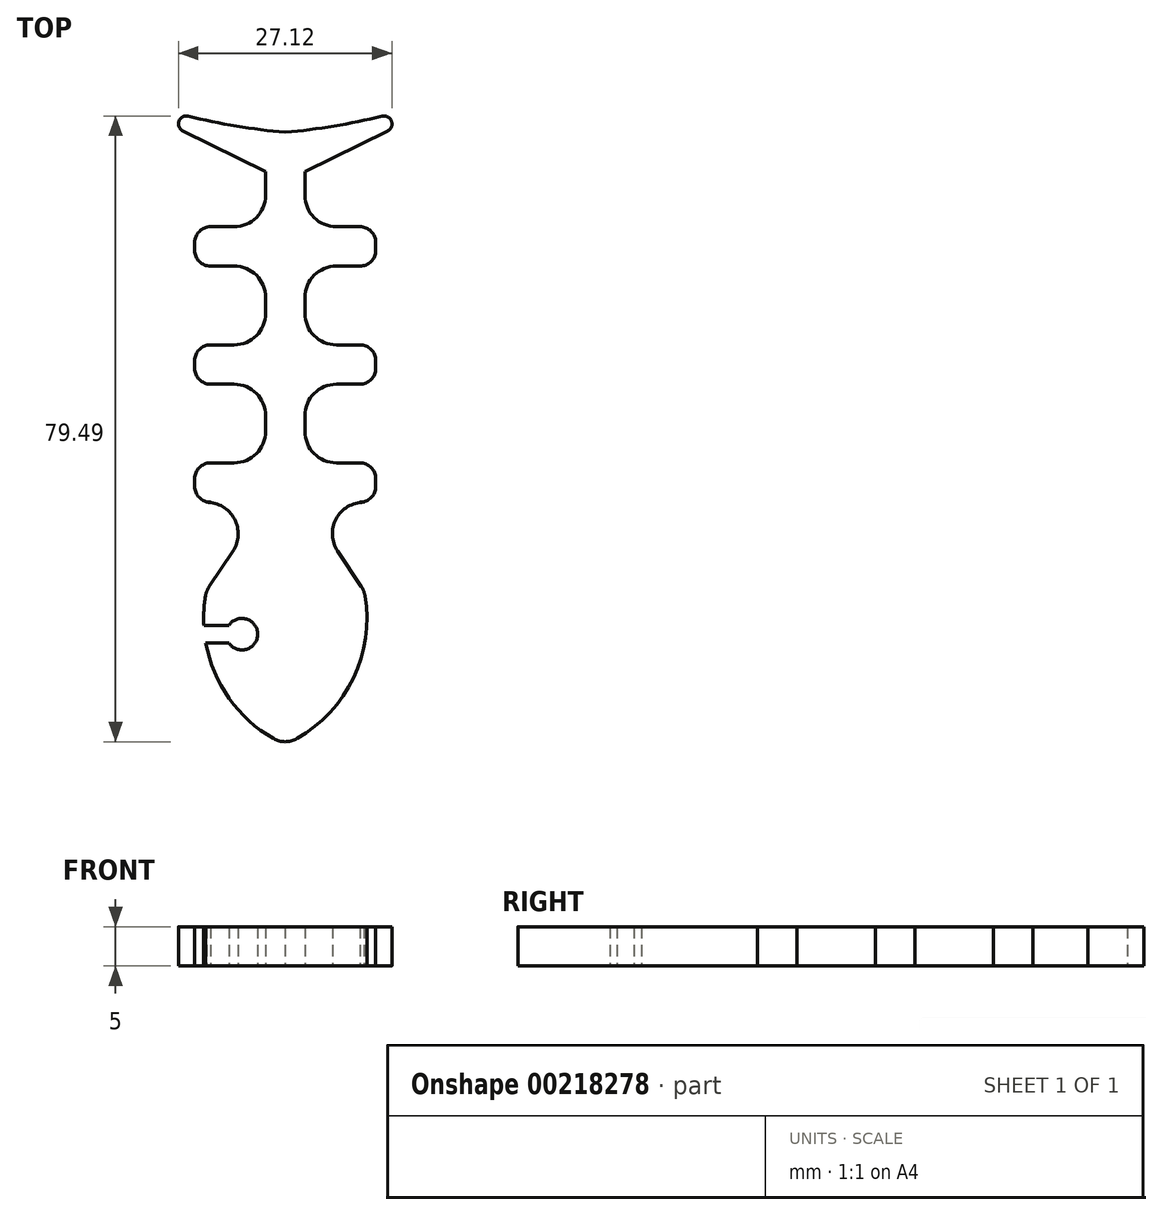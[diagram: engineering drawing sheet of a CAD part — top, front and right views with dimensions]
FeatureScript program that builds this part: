
annotation { "Feature Type Name" : "Feature", "Feature Type Description" : "" }
export const myFeature = defineFeature(function(context is Context, id is Id, definition is map)
    precondition{}
    {
        {
            var Q0;
            Q0=qCreatedBy(makeId("Top.planeOp"),FACE);
            var sketch = newSketch(context, id + "F0", { "sketchPlane" : qUnion([Q0])});
            skLineSegment(sketch, "E0", {"start": v(0, -19.65) * mm, "end": v(0, 37) * mm});
            skLineSegment(sketch, "E1", {"start": v(-9.66, -15.71) * mm, "end": v(-6.66, -11.22) * mm});
            skLineSegment(sketch, "E2", {"start": v(-9.5, -5) * mm, "end": v(-9.98, -5) * mm});
            skLineSegment(sketch, "E3", {"start": v(-11.5, -3) * mm, "end": v(-11.5, -2) * mm});
            skLineSegment(sketch, "E4", {"start": v(-9.5, 0) * mm, "end": v(-6.5, 0) * mm});
            skLineSegment(sketch, "E5", {"start": v(-2.5, 4) * mm, "end": v(-2.5, 6) * mm});
            skLineSegment(sketch, "E6", {"start": v(-6.5, 10) * mm, "end": v(-9.5, 10) * mm});
            skLineSegment(sketch, "E7", {"start": v(-11.5, 12) * mm, "end": v(-11.5, 13) * mm});
            skLineSegment(sketch, "E8", {"start": v(-9.5, 15) * mm, "end": v(-6.5, 15) * mm});
            skLineSegment(sketch, "E9", {"start": v(-2.5, 19) * mm, "end": v(-2.5, 21) * mm});
            skLineSegment(sketch, "E10", {"start": v(-6.5, 25) * mm, "end": v(-9.5, 25) * mm});
            skLineSegment(sketch, "E11", {"start": v(-11.5, 27) * mm, "end": v(-11.5, 28) * mm});
            skLineSegment(sketch, "E12", {"start": v(-9.5, 30) * mm, "end": v(-6.5, 30) * mm});
            skLineSegment(sketch, "E13", {"start": v(-2.5, 34) * mm, "end": v(-2.5, 37) * mm});
            skLineSegment(sketch, "E14", {"start": v(-2.5, 37) * mm, "end": v(-13, 42.17) * mm});
            skLineSegment(sketch, "E15", {"start": v(0, 37) * mm, "end": v(0, 42) * mm});
            skArc(sketch, "E16", {"start": v(-12.32, 44.04) * mm, "mid": v(-6.2, 42.79) * mm, "end": v(0, 42) * mm});
            skLineSegment(sketch, "E17", {"start": v(0, -19.65) * mm, "end": v(0, -23.17) * mm});
            skPoint(sketch, "E18.visualSharp", {"position": v(-2.5, 30) * mm});
            skArc(sketch, "E18.filletArc", {"start": v(-6.5, 30) * mm, "mid": v(-3.67, 31.17) * mm, "end": v(-2.5, 34) * mm});
            skPoint(sketch, "E19.visualSharp", {"position": v(-2.5, 25) * mm});
            skArc(sketch, "E19.filletArc", {"start": v(-2.5, 21) * mm, "mid": v(-3.67, 23.83) * mm, "end": v(-6.5, 25) * mm});
            skPoint(sketch, "E20.visualSharp", {"position": v(-2.5, 15) * mm});
            skArc(sketch, "E20.filletArc", {"start": v(-6.5, 15) * mm, "mid": v(-3.67, 16.17) * mm, "end": v(-2.5, 19) * mm});
            skPoint(sketch, "E21.visualSharp", {"position": v(-2.5, 10) * mm});
            skArc(sketch, "E21.filletArc", {"start": v(-2.5, 6) * mm, "mid": v(-3.67, 8.83) * mm, "end": v(-6.5, 10) * mm});
            skPoint(sketch, "E22.visualSharp", {"position": v(-2.5, 0) * mm});
            skArc(sketch, "E22.filletArc", {"start": v(-6.5, 0) * mm, "mid": v(-3.67, 1.17) * mm, "end": v(-2.5, 4) * mm});
            skPoint(sketch, "E23.visualSharp", {"position": v(-2.5, -5) * mm});
            skArc(sketch, "E23.filletArc", {"start": v(-6.66, -11.22) * mm, "mid": v(-6.46, -7.11) * mm, "end": v(-9.98, -5) * mm});
            skPoint(sketch, "E24.visualSharp", {"position": v(-11.5, 30) * mm});
            skArc(sketch, "E24.filletArc", {"start": v(-9.5, 30) * mm, "mid": v(-10.91, 29.41) * mm, "end": v(-11.5, 28) * mm});
            skPoint(sketch, "E25.visualSharp", {"position": v(-11.5, 15) * mm});
            skArc(sketch, "E25.filletArc", {"start": v(-9.5, 15) * mm, "mid": v(-10.91, 14.41) * mm, "end": v(-11.5, 13) * mm});
            skPoint(sketch, "E26.visualSharp", {"position": v(-11.5, 0) * mm});
            skArc(sketch, "E26.filletArc", {"start": v(-9.5, 0) * mm, "mid": v(-10.91, -0.59) * mm, "end": v(-11.5, -2) * mm});
            skPoint(sketch, "E27.visualSharp", {"position": v(-11.5, 25) * mm});
            skArc(sketch, "E27.filletArc", {"start": v(-11.5, 27) * mm, "mid": v(-10.91, 25.59) * mm, "end": v(-9.5, 25) * mm});
            skPoint(sketch, "E28.visualSharp", {"position": v(-11.5, 10) * mm});
            skArc(sketch, "E28.filletArc", {"start": v(-11.5, 12) * mm, "mid": v(-10.91, 10.59) * mm, "end": v(-9.5, 10) * mm});
            skPoint(sketch, "E29.visualSharp", {"position": v(-11.5, -5) * mm});
            skArc(sketch, "E29.filletArc", {"start": v(-11.5, -3) * mm, "mid": v(-10.91, -4.41) * mm, "end": v(-9.5, -5) * mm});
            skPoint(sketch, "E30.visualSharp", {"position": v(-28.2, 49.66) * mm});
            skArc(sketch, "E30.filletArc", {"start": v(-12.32, 44.04) * mm, "mid": v(-13.5, 43.41) * mm, "end": v(-13, 42.17) * mm});
            skArc(sketch, "E31.MirrorCS", {"start": v(9.5, 0) * mm, "mid": v(10.91, -0.59) * mm, "end": v(11.5, -2) * mm});
            skLineSegment(sketch, "E32.MirrorCS", {"start": v(11.5, 27) * mm, "end": v(11.5, 28) * mm});
            skLineSegment(sketch, "E33.MirrorCS", {"start": v(9.5, -5) * mm, "end": v(9.98, -5) * mm});
            skLineSegment(sketch, "E34.MirrorCS", {"start": v(11.5, 12) * mm, "end": v(11.5, 13) * mm});
            skLineSegment(sketch, "E35.MirrorCS", {"start": v(2.5, 4) * mm, "end": v(2.5, 6) * mm});
            skArc(sketch, "E36.MirrorCS", {"start": v(11.5, 12) * mm, "mid": v(10.91, 10.59) * mm, "end": v(9.5, 10) * mm});
            skArc(sketch, "E37.MirrorCS", {"start": v(11.5, -3) * mm, "mid": v(10.91, -4.41) * mm, "end": v(9.5, -5) * mm});
            skArc(sketch, "E38.MirrorCS", {"start": v(9.5, 30) * mm, "mid": v(10.91, 29.41) * mm, "end": v(11.5, 28) * mm});
            skLineSegment(sketch, "E39.MirrorCS", {"start": v(11.5, -3) * mm, "end": v(11.5, -2) * mm});
            skLineSegment(sketch, "E40.MirrorCS", {"start": v(2.5, 34) * mm, "end": v(2.5, 37) * mm});
            skArc(sketch, "E41.MirrorCS", {"start": v(12.32, 44.04) * mm, "mid": v(13.5, 43.41) * mm, "end": v(13, 42.17) * mm});
            skArc(sketch, "E42.MirrorCS", {"start": v(9.5, 15) * mm, "mid": v(10.91, 14.41) * mm, "end": v(11.5, 13) * mm});
            skLineSegment(sketch, "E43.MirrorCS", {"start": v(9.5, 15) * mm, "end": v(6.5, 15) * mm});
            skLineSegment(sketch, "E44.MirrorCS", {"start": v(6.5, 25) * mm, "end": v(9.5, 25) * mm});
            skLineSegment(sketch, "E45.MirrorCS", {"start": v(2.5, 19) * mm, "end": v(2.5, 21) * mm});
            skArc(sketch, "E46.MirrorCS", {"start": v(11.5, 27) * mm, "mid": v(10.91, 25.59) * mm, "end": v(9.5, 25) * mm});
            skLineSegment(sketch, "E47.MirrorCS", {"start": v(9.5, 30) * mm, "end": v(6.5, 30) * mm});
            skLineSegment(sketch, "E48.MirrorCS", {"start": v(6.5, 10) * mm, "end": v(9.5, 10) * mm});
            skLineSegment(sketch, "E49.MirrorCS", {"start": v(9.5, 0) * mm, "end": v(6.5, 0) * mm});
            skArc(sketch, "E50.MirrorCS", {"start": v(2.5, 21) * mm, "mid": v(3.67, 23.83) * mm, "end": v(6.5, 25) * mm});
            skArc(sketch, "E51.MirrorCS", {"start": v(6.5, 30) * mm, "mid": v(3.67, 31.17) * mm, "end": v(2.5, 34) * mm});
            skArc(sketch, "E52.MirrorCS", {"start": v(6.5, 0) * mm, "mid": v(3.67, 1.17) * mm, "end": v(2.5, 4) * mm});
            skArc(sketch, "E53.MirrorCS", {"start": v(6.66, -11.22) * mm, "mid": v(6.46, -7.11) * mm, "end": v(9.98, -5) * mm});
            skArc(sketch, "E54.MirrorCS", {"start": v(2.5, 6) * mm, "mid": v(3.67, 8.83) * mm, "end": v(6.5, 10) * mm});
            skArc(sketch, "E55.MirrorCS", {"start": v(6.5, 15) * mm, "mid": v(3.67, 16.17) * mm, "end": v(2.5, 19) * mm});
            skPoint(sketch, "E56.MirrorP", {"position": v(2.5, 25) * mm});
            skPoint(sketch, "E57.MirrorP", {"position": v(2.5, 0) * mm});
            skLineSegment(sketch, "E58.MirrorCS", {"start": v(2.5, 37) * mm, "end": v(13, 42.17) * mm});
            skPoint(sketch, "E59.MirrorP", {"position": v(11.5, 25) * mm});
            skPoint(sketch, "E60.MirrorP", {"position": v(11.5, 15) * mm});
            skLineSegment(sketch, "E61.MirrorCS", {"start": v(9.66, -15.71) * mm, "end": v(6.66, -11.22) * mm});
            skArc(sketch, "E62.MirrorCS", {"start": v(12.32, 44.04) * mm, "mid": v(6.2, 42.79) * mm, "end": v(0, 42) * mm});
            skPoint(sketch, "E63.MirrorP", {"position": v(11.5, -5) * mm});
            skPoint(sketch, "E64.MirrorP", {"position": v(2.5, 15) * mm});
            skPoint(sketch, "E65.MirrorP", {"position": v(2.5, 30) * mm});
            skPoint(sketch, "E66.MirrorP", {"position": v(11.5, 0) * mm});
            skPoint(sketch, "E67.MirrorP", {"position": v(11.5, 10) * mm});
            skPoint(sketch, "E68.MirrorP", {"position": v(2.5, 10) * mm});
            skPoint(sketch, "E69.MirrorP", {"position": v(2.5, -5) * mm});
            skPoint(sketch, "E70.MirrorP", {"position": v(11.5, 30) * mm});
            skArc(sketch, "E71", {"start": v(-10.12, -16.89) * mm, "mid": v(-10.33, -18.76) * mm, "end": v(-10.34, -20.65) * mm});
            skArc(sketch, "E72.MirrorCS", {"start": v(10.12, -16.89) * mm, "mid": v(8.66, -27.32) * mm, "end": v(1.48, -35.03) * mm});
            skPoint(sketch, "E73.visualSharp", {"position": v(0, -35.78) * mm});
            skArc(sketch, "E73.filletArc", {"start": v(-1.48, -35.03) * mm, "mid": v(0, -35.42) * mm, "end": v(1.48, -35.03) * mm});
            skPoint(sketch, "E74.visualSharp", {"position": v(10, -16.22) * mm});
            skArc(sketch, "E74.filletArc", {"start": v(10.12, -16.89) * mm, "mid": v(9.95, -16.27) * mm, "end": v(9.66, -15.71) * mm});
            skPoint(sketch, "E75.visualSharp", {"position": v(-10, -16.22) * mm});
            skArc(sketch, "E75.filletArc", {"start": v(-9.66, -15.71) * mm, "mid": v(-9.95, -16.27) * mm, "end": v(-10.12, -16.89) * mm});
            skArc(sketch, "E76", {"start": v(-7.16, -22.87) * mm, "mid": v(-3.5, -21.76) * mm, "end": v(-7.16, -20.65) * mm});
            skLineSegment(sketch, "E77", {"start": v(-7.16, -20.65) * mm, "end": v(-10.34, -20.65) * mm});
            skLineSegment(sketch, "E78", {"start": v(-7.16, -22.87) * mm, "end": v(-10.09, -22.87) * mm});
            skArc(sketch, "E79.trimOffspring", {"start": v(-10.09, -22.87) * mm, "mid": v(-7.14, -29.9) * mm, "end": v(-1.48, -35.03) * mm});
            skSolve(sketch);
        }
        {
            var Q0;
            Q0=makeQuery(id+"F0.imprint","IMPRINT",FACE,{"disambiguationData":[TD([[makeQuery(id+"F0.imprint","IMPRINT",EDGE,{"derivedFrom":sQuery(id+"F0.wireOp",EDGE,"E1")}),-1.0]])]});
            extrude(context, id + "F1", {"entities" : qUnion([Q0]), "depth" : 5 * mm});
        }
    });
